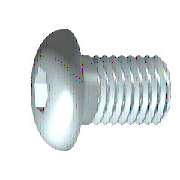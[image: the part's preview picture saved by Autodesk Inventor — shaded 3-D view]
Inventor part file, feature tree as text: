
AUTODESK INVENTOR PART (.ipt)
format: ipt  version: 2024.1 (Build 281209000, 209)  size: 186,880 bytes
history: native  units: mm (DEFAULTED — no unit token found)
features: extrude x1, plane x1, fillet x1, thread x1
ambient origin geometry x7: Origin, YZ Plane, XY Plane, X Axis, Y Axis, Z Axis, Center Point
bodies: Solid1 (feature_tree), Body (feature_tree)
feature tree (4):
  extrude  "Slot"  Depth=4.5mm
  plane  "Work Plane1"
  fillet  "Fillet2"  Radius=0.306825mm
  thread  "Thread2"  [1 undecoded]
note: 1 required parameter value undecoded (feature->parameter linkage not recoverable at this tier; creation-order binding heuristic only, values carry confidence <= 0.55)
